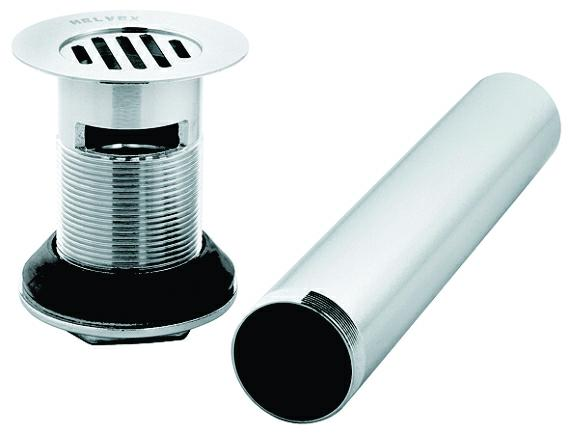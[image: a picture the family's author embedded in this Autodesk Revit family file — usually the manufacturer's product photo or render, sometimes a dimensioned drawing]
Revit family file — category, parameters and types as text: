
# Revit family: TH-058_RFA
name_source: partatom
category: Aparatos sanitarios
units: mm (PartAtom-declared; Revit-internal decimal feet)

## family parameters
Activar corte en vistas = No
Compartido = Sí
Corte con vacíos al cargar = No
Cota de conector redondo = Usar diámetro
Mantener orientación de anotación = No
Número OmniClass = 23.45.05.14.99
Punto de cálculo de habitación = Sí
Se basa en plano de trabajo = No
Siempre vertical = Sí
Tipo de pieza = Normal
Título OmniClass = Other Sanitary Washing Plumbing Fixtures

## types (1)
- TH-058
    Brass Chromed = Brass
    Comentarios de tipo = Lavatory Accesories
    Data Sheet = http://www.helvex.com.mx
    Descripción = Lavatory Grid Drain With Overflow
    Elevación por Defecto = 0"
    Elevación por defecto = 0"
    Fabricante = HELVEX
    Features = Fixed Grid; With Overflow
    Imagen de tipo = TH-058.jpg
    Inlet Threads = 1 ¼" Pipe
    Modelo = TH-058
    Total Diameter = 2"
    Total Height = 10"
    URL = http://www.helvex.com.mx

## geometry (parser evidence)
native form markers: Sweep x3
no freeform markers — native parametric forms only
